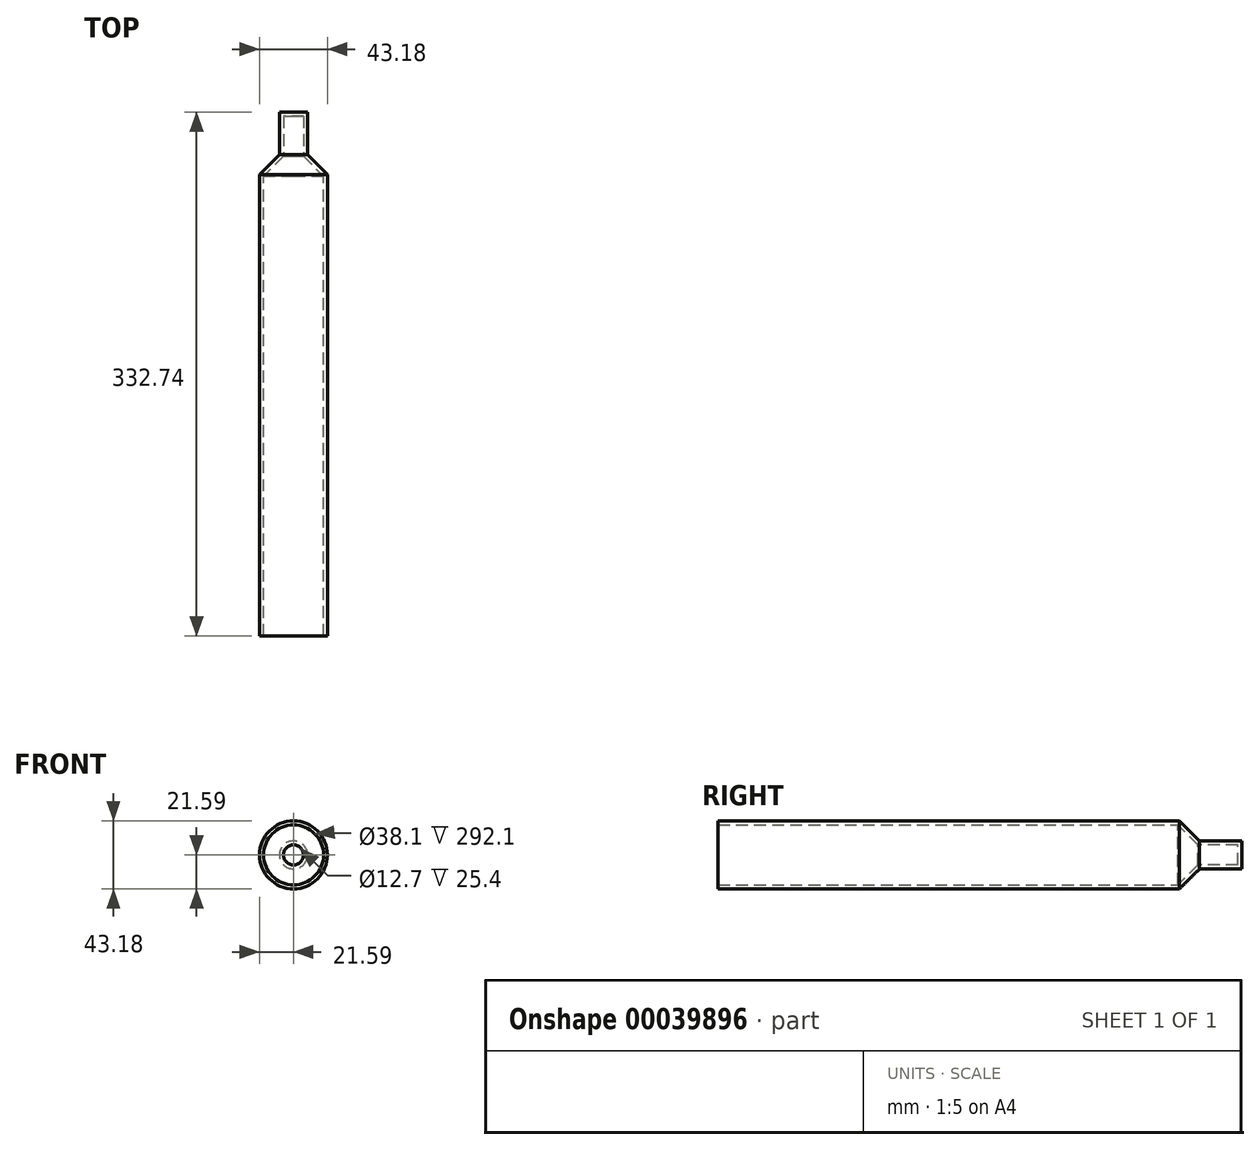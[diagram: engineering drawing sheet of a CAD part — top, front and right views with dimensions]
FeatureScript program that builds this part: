
annotation { "Feature Type Name" : "Feature", "Feature Type Description" : "" }
export const myFeature = defineFeature(function(context is Context, id is Id, definition is map)
    precondition{}
    {
        {
            var Q0;
            Q0=qCreatedBy(makeId("Front.planeOp"),FACE);
            var sketch = newSketch(context, id + "F0", { "sketchPlane" : qUnion([Q0])});
            skCircle(sketch, "E0", {"center": v(0, 0) * mm, "radius": 19.05 * mm});
            skSolve(sketch);
        }
        {
            var Q0;
            Q0=makeQuery(id+"F0.imprint","IMPRINT",FACE,{"disambiguationData":[TD([[makeQuery(id+"F0.imprint","IMPRINT",EDGE,{"derivedFrom":sQuery(id+"F0.wireOp",EDGE,"E0")}),1.0]])]});
            extrude(context, id + "F1", {"entities" : qUnion([Q0]), "depth" : 304.8 * mm});
        }
        {
            var Q0;
            Q0=makeQuery(id+"F1.opExtrude","CAP_FACE",FACE,{"disambiguationData":[OSD([sQuery(id+"F0.wireOp",EDGE,"E0")])],"isStart":false});
            var sketch = newSketch(context, id + "F2", { "sketchPlane" : qUnion([Q0])});
            skSolve(sketch);
        }
        {
            var Q0;
            Q0=makeQuery(id+"F1.opExtrude","CAP_EDGE",EDGE,{"disambiguationData":[OSD([sQuery(id+"F0.wireOp",EDGE,"E0")])],"isStart":true});
            chamfer(context, id + "F3", {"entities" : qUnion([Q0]), "width" : 12.7 * mm, "tangentPropagation" : true});
        }
        {
            var Q0;
            Q0=makeQuery(id+"F1.opExtrude","CAP_FACE",FACE,{"disambiguationData":[OSD([sQuery(id+"F0.wireOp",EDGE,"E0")])],"isStart":true});
            extrude(context, id + "F4", {"entities" : qUnion([Q0]), "operationType" : NewBodyOperationType.ADD, "depth" : 25.4 * mm});
        }
        {
            var Q0;
            Q0=makeQuery(id+"F1.opExtrude","CAP_FACE",FACE,{"disambiguationData":[OSD([sQuery(id+"F0.wireOp",EDGE,"E0")])],"isStart":false});
            shell(context, id + "F5", {"entities" : qUnion([Q0]), "thickness" : 2.54 * mm, "oppositeDirection" : true});
        }
        {
            var Q0;
            Q0=makeQuery(id+"F2.imprint","IMPRINT",FACE,{"disambiguationData":[TD([[makeQuery(id+"F2.imprint","IMPRINT",EDGE,{"derivedFrom":makeQuery(id+"F1.opExtrude","CAP_EDGE",EDGE,{"disambiguationData":[OSD([sQuery(id+"F0.wireOp",EDGE,"E0")])],"isStart":false})}),1.0]])]});
            var sketch = newSketch(context, id + "F6", { "sketchPlane" : qUnion([Q0])});
            skLineSegment(sketch, "E1.rect.bottom", {"start": v(15.88, 9.53) * mm, "end": v(-15.88, 9.53) * mm});
            skLineSegment(sketch, "E1.rect.top", {"start": v(15.88, -9.53) * mm, "end": v(-15.88, -9.53) * mm});
            skLineSegment(sketch, "E1.rect.left", {"start": v(15.88, 9.53) * mm, "end": v(15.88, -9.53) * mm});
            skLineSegment(sketch, "E1.rect.right", {"start": v(-15.88, 9.53) * mm, "end": v(-15.88, -9.53) * mm});
            skPoint(sketch, "E1.rect.middle", {"position": v(0, 0) * mm});
            skSolve(sketch);
        }
        {
            var Q0;
            Q0=makeQuery(id+"F6.imprint","IMPRINT",FACE,{"disambiguationData":[TD([[makeQuery(id+"F6.imprint","IMPRINT",EDGE,{"derivedFrom":sQuery(id+"F6.wireOp",EDGE,"E1.rect.bottom")}),1.0]])]});
            extrude(context, id + "F7", {"entities" : qUnion([Q0]), "depth" : 5.08 * mm});
        }
        {
            var Q0;
            Q0=makeQuery(id+"F7.opExtrude","CAP_FACE",FACE,{"disambiguationData":[OSD([sQuery(id+"F6.wireOp",EDGE,"E1.rect.bottom"),sQuery(id+"F6.wireOp",EDGE,"E1.rect.top"),sQuery(id+"F6.wireOp",EDGE,"E1.rect.left"),sQuery(id+"F6.wireOp",EDGE,"E1.rect.right")])],"isStart":false});
            var sketch = newSketch(context, id + "F8", { "sketchPlane" : qUnion([Q0])});
            skCircle(sketch, "E2", {"center": v(0, 0) * mm, "radius": 9.75 * mm});
            skSolve(sketch);
        }
        {
            var Q0;
            Q0 = qSketchRegion(id + "F8", true);
            extrude(context, id + "F9", {"entities" : qUnion([Q0]), "oppositeDirection" : true, "depth" : 25.4 * mm});
        }
        {
            var Q0;
            Q0=makeQuery(id+"F9.opExtrude","SWEPT_BODY",BODY,{"disambiguationData":[OSD([sQuery(id+"F8.wireOp",EDGE,"E2")])]});
            deleteBodies(context, id + "F10", {"entities" : qUnion([Q0])});
        }
        {
            var Q0;
            Q0=makeQuery(id+"F7.opExtrude","SWEPT_BODY",BODY,{"disambiguationData":[OSD([sQuery(id+"F6.wireOp",EDGE,"E1.rect.bottom"),sQuery(id+"F6.wireOp",EDGE,"E1.rect.top"),sQuery(id+"F6.wireOp",EDGE,"E1.rect.left"),sQuery(id+"F6.wireOp",EDGE,"E1.rect.right")])]});
            deleteBodies(context, id + "F11", {"entities" : qUnion([Q0])});
        }
    });
